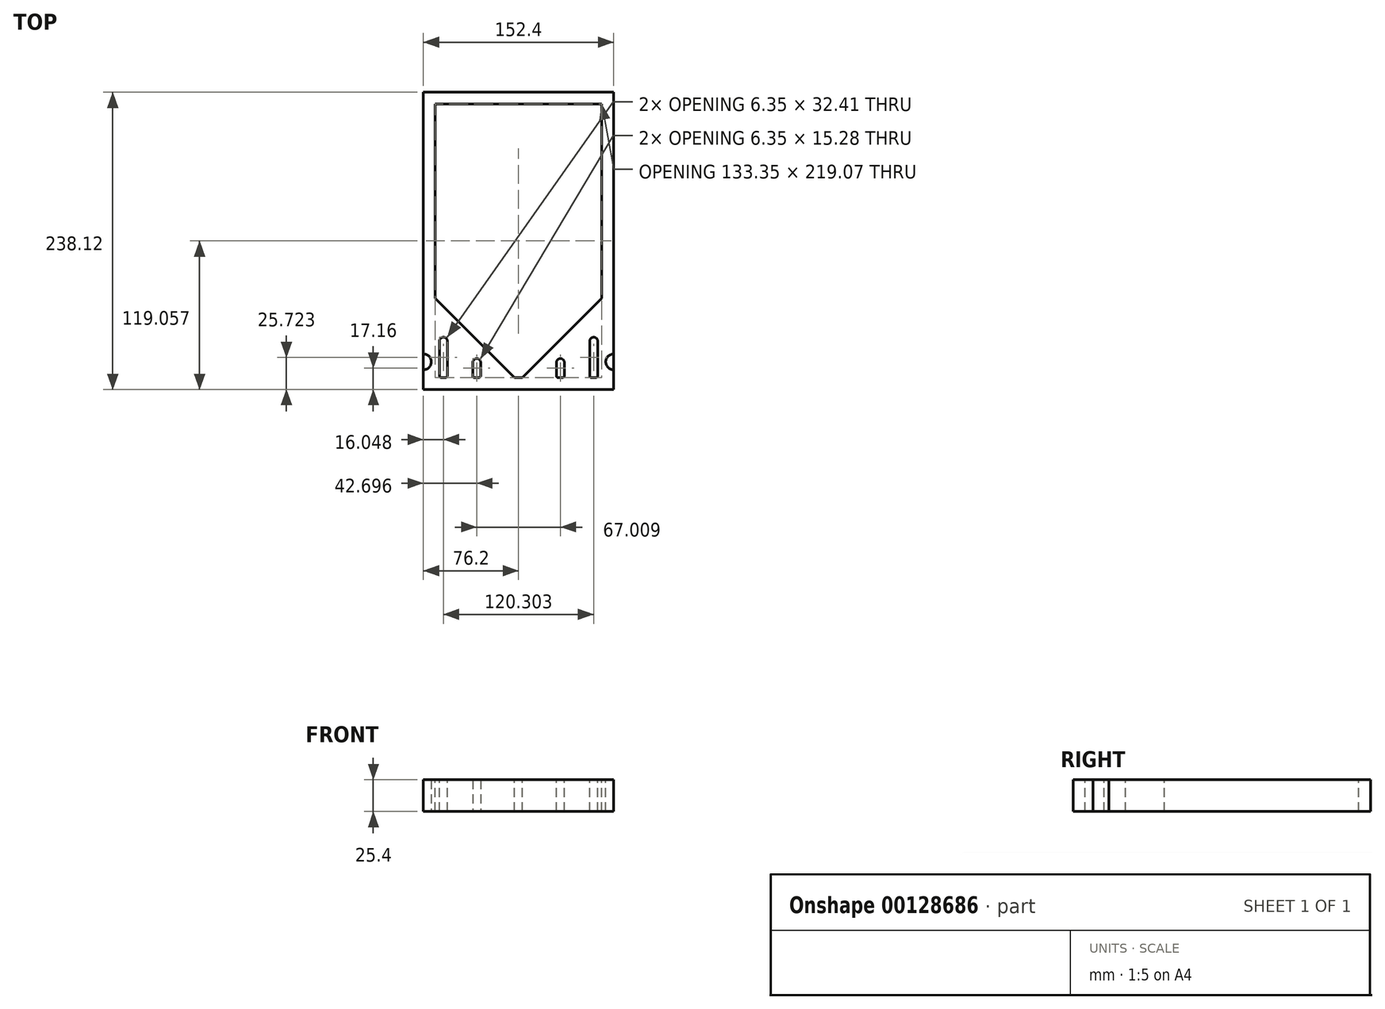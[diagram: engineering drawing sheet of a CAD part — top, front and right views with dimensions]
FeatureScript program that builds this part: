
annotation { "Feature Type Name" : "Feature", "Feature Type Description" : "" }
export const myFeature = defineFeature(function(context is Context, id is Id, definition is map)
    precondition{}
    {
        {
            var Q0;
            Q0=qCreatedBy(makeId("Top.planeOp"),FACE);
            var sketch = newSketch(context, id + "F0", { "sketchPlane" : qUnion([Q0])});
            skLineSegment(sketch, "E0", {"start": v(-76.2, 128.27) * mm, "end": v(-76.2, -109.86) * mm});
            skLineSegment(sketch, "E1", {"start": v(-76.2, -109.86) * mm, "end": v(76.2, -109.86) * mm});
            skLineSegment(sketch, "E2", {"start": v(76.2, -109.86) * mm, "end": v(76.2, 128.27) * mm});
            skLineSegment(sketch, "E3", {"start": v(76.2, 128.27) * mm, "end": v(-76.2, 128.27) * mm});
            skLineSegment(sketch, "E4.1", {"start": v(66.67, 118.75) * mm, "end": v(-66.67, 118.74) * mm});
            skLineSegment(sketch, "E5", {"start": v(-3.17, -100.33) * mm, "end": v(-66.68, -36.83) * mm});
            skLineSegment(sketch, "E6", {"start": v(-66.67, -36.83) * mm, "end": v(-66.67, 118.74) * mm});
            skLineSegment(sketch, "E7", {"start": v(66.67, 118.75) * mm, "end": v(66.67, -36.83) * mm});
            skLineSegment(sketch, "E8.MirrorCS", {"start": v(3.17, -100.33) * mm, "end": v(66.67, -36.83) * mm});
            skLineSegment(sketch, "E9", {"start": v(-3.17, -100.33) * mm, "end": v(3.17, -100.33) * mm});
            skArc(sketch, "E10", {"start": v(-76.2, -93.98) * mm, "mid": v(-69.85, -87.63) * mm, "end": v(-76.2, -81.28) * mm});
            skLineSegment(sketch, "E11", {"start": v(-56.98, -98.74) * mm, "end": v(-56.98, -71.1) * mm});
            skLineSegment(sketch, "E12.0", {"start": v(-63.33, -98.74) * mm, "end": v(-63.33, -71.1) * mm});
            skLineSegment(sketch, "E13.0", {"start": v(-30.33, -98.74) * mm, "end": v(-30.33, -88.22) * mm});
            skLineSegment(sketch, "E14.0", {"start": v(-36.68, -98.74) * mm, "end": v(-36.68, -88.22) * mm});
            skLineSegment(sketch, "E15", {"start": v(-61.74, -100.33) * mm, "end": v(-58.56, -100.33) * mm});
            skLineSegment(sketch, "E16", {"start": v(-35.1, -100.33) * mm, "end": v(-31.92, -100.33) * mm});
            skArc(sketch, "E17", {"start": v(-56.98, -71.1) * mm, "mid": v(-60.15, -67.92) * mm, "end": v(-63.33, -71.1) * mm});
            skArc(sketch, "E18", {"start": v(-30.33, -88.22) * mm, "mid": v(-33.5, -85.05) * mm, "end": v(-36.68, -88.22) * mm});
            skLineSegment(sketch, "E19.MirrorCS", {"start": v(36.68, -98.74) * mm, "end": v(36.68, -88.22) * mm});
            skLineSegment(sketch, "E20.MirrorCS", {"start": v(30.33, -98.74) * mm, "end": v(30.33, -88.22) * mm});
            skLineSegment(sketch, "E21.MirrorCS", {"start": v(35.1, -100.33) * mm, "end": v(31.92, -100.33) * mm});
            skArc(sketch, "E22.MirrorCS", {"start": v(30.33, -88.22) * mm, "mid": v(33.5, -85.05) * mm, "end": v(36.68, -88.22) * mm});
            skLineSegment(sketch, "E23.MirrorCS", {"start": v(56.98, -98.74) * mm, "end": v(56.98, -71.1) * mm});
            skLineSegment(sketch, "E24.MirrorCS", {"start": v(63.33, -98.74) * mm, "end": v(63.33, -71.1) * mm});
            skLineSegment(sketch, "E25.MirrorCS", {"start": v(61.74, -100.33) * mm, "end": v(58.56, -100.33) * mm});
            skArc(sketch, "E26.MirrorCS", {"start": v(56.98, -71.1) * mm, "mid": v(60.15, -67.92) * mm, "end": v(63.33, -71.1) * mm});
            skLineSegment(sketch, "E27", {"start": v(0, -100.33) * mm, "end": v(0, -87.84) * mm});
            skArc(sketch, "E28.MirrorCS", {"start": v(76.2, -93.98) * mm, "mid": v(69.85, -87.63) * mm, "end": v(76.2, -81.28) * mm});
            skPoint(sketch, "E29.visualSharp", {"position": v(-63.33, -100.33) * mm});
            skArc(sketch, "E29.filletArc", {"start": v(-63.33, -98.74) * mm, "mid": v(-62.86, -99.87) * mm, "end": v(-61.74, -100.33) * mm});
            skPoint(sketch, "E30.visualSharp", {"position": v(-56.98, -100.33) * mm});
            skArc(sketch, "E30.filletArc", {"start": v(-58.56, -100.33) * mm, "mid": v(-57.44, -99.87) * mm, "end": v(-56.98, -98.74) * mm});
            skPoint(sketch, "E31.visualSharp", {"position": v(-36.68, -100.33) * mm});
            skArc(sketch, "E31.filletArc", {"start": v(-36.68, -98.74) * mm, "mid": v(-36.21, -99.87) * mm, "end": v(-35.1, -100.33) * mm});
            skPoint(sketch, "E32.visualSharp", {"position": v(-30.33, -100.33) * mm});
            skArc(sketch, "E32.filletArc", {"start": v(-31.92, -100.33) * mm, "mid": v(-30.8, -99.87) * mm, "end": v(-30.33, -98.74) * mm});
            skPoint(sketch, "E33.visualSharp", {"position": v(30.33, -100.33) * mm});
            skArc(sketch, "E33.filletArc", {"start": v(30.33, -98.74) * mm, "mid": v(30.8, -99.87) * mm, "end": v(31.92, -100.33) * mm});
            skPoint(sketch, "E34.visualSharp", {"position": v(36.68, -100.33) * mm});
            skArc(sketch, "E34.filletArc", {"start": v(35.1, -100.33) * mm, "mid": v(36.21, -99.87) * mm, "end": v(36.68, -98.74) * mm});
            skPoint(sketch, "E35.visualSharp", {"position": v(56.98, -100.33) * mm});
            skArc(sketch, "E35.filletArc", {"start": v(56.98, -98.74) * mm, "mid": v(57.44, -99.87) * mm, "end": v(58.56, -100.33) * mm});
            skPoint(sketch, "E36.visualSharp", {"position": v(63.33, -100.33) * mm});
            skArc(sketch, "E36.filletArc", {"start": v(61.74, -100.33) * mm, "mid": v(62.86, -99.87) * mm, "end": v(63.33, -98.74) * mm});
            skSolve(sketch);
        }
        {
            var Q0;
            {var subQ5=sQuery(id+"F0.wireOp",EDGE,"E1");Q0=makeQuery(id+"F0.imprint","IMPRINT",FACE,{"disambiguationData":[TD([[makeQuery(id+"F0.imprint","IMPRINT",EDGE,{"derivedFrom":subQ5}),1.0]])]});}
            var Q1;
            Q1 = qConstructionFilter(qBodyType(qCreatedBy(id + "F0" ,EDGE), BodyType.WIRE), ConstructionObject.NO);
            extrude(context, id + "F1", {"entities" : qUnion([Q0]), "surfaceEntities" : qUnion([Q1]), "depth" : 25.4 * mm});
        }
        {
            var Q0;
            Q0=makeQuery(id+"F1.opExtrude","CAP_FACE",FACE,{"disambiguationData":[OSD([sQuery(id+"F0.wireOp",EDGE,"E0"),sQuery(id+"F0.wireOp",EDGE,"E1"),sQuery(id+"F0.wireOp",EDGE,"E2"),sQuery(id+"F0.wireOp",EDGE,"E3"),sQuery(id+"F0.wireOp",EDGE,"E4.1"),sQuery(id+"F0.wireOp",EDGE,"E5"),sQuery(id+"F0.wireOp",EDGE,"E6"),sQuery(id+"F0.wireOp",EDGE,"E7"),sQuery(id+"F0.wireOp",EDGE,"E8.MirrorCS"),sQuery(id+"F0.wireOp",EDGE,"E9"),sQuery(id+"F0.wireOp",EDGE,"E10"),sQuery(id+"F0.wireOp",EDGE,"E11"),sQuery(id+"F0.wireOp",EDGE,"E12.0"),sQuery(id+"F0.wireOp",EDGE,"E13.0"),sQuery(id+"F0.wireOp",EDGE,"E14.0"),sQuery(id+"F0.wireOp",EDGE,"E15"),sQuery(id+"F0.wireOp",EDGE,"E16"),sQuery(id+"F0.wireOp",EDGE,"E17"),sQuery(id+"F0.wireOp",EDGE,"E18"),sQuery(id+"F0.wireOp",EDGE,"E19.MirrorCS"),sQuery(id+"F0.wireOp",EDGE,"E20.MirrorCS"),sQuery(id+"F0.wireOp",EDGE,"E21.MirrorCS"),sQuery(id+"F0.wireOp",EDGE,"E22.MirrorCS"),sQuery(id+"F0.wireOp",EDGE,"E23.MirrorCS"),sQuery(id+"F0.wireOp",EDGE,"E24.MirrorCS"),sQuery(id+"F0.wireOp",EDGE,"E25.MirrorCS"),sQuery(id+"F0.wireOp",EDGE,"E26.MirrorCS"),sQuery(id+"F0.wireOp",EDGE,"E28.MirrorCS"),sQuery(id+"F0.wireOp",EDGE,"E29.filletArc"),sQuery(id+"F0.wireOp",EDGE,"E30.filletArc"),sQuery(id+"F0.wireOp",EDGE,"E31.filletArc"),sQuery(id+"F0.wireOp",EDGE,"E32.filletArc"),sQuery(id+"F0.wireOp",EDGE,"E33.filletArc"),sQuery(id+"F0.wireOp",EDGE,"E34.filletArc"),sQuery(id+"F0.wireOp",EDGE,"E35.filletArc"),sQuery(id+"F0.wireOp",EDGE,"E36.filletArc")])],"isStart":false});
            var sketch = newSketch(context, id + "F2", { "sketchPlane" : qUnion([Q0])});
            skLineSegment(sketch, "E37.0", {"start": v(-3.17, -100.33) * mm, "end": v(-66.67, -36.83) * mm});
            skLineSegment(sketch, "E37.1", {"start": v(-66.67, -36.83) * mm, "end": v(-66.67, 118.74) * mm});
            skLineSegment(sketch, "E37.2", {"start": v(-3.17, -100.33) * mm, "end": v(3.17, -100.33) * mm});
            skLineSegment(sketch, "E37.3", {"start": v(3.17, -100.33) * mm, "end": v(66.67, -36.83) * mm});
            skLineSegment(sketch, "E37.4", {"start": v(66.67, 118.75) * mm, "end": v(66.67, -36.83) * mm});
            skLineSegment(sketch, "E37.5", {"start": v(66.67, 118.75) * mm, "end": v(-66.67, 118.74) * mm});
            skLineSegment(sketch, "E37.6", {"start": v(-63.33, -98.74) * mm, "end": v(-63.33, -71.1) * mm});
            skLineSegment(sketch, "E37.7", {"start": v(-56.98, -98.74) * mm, "end": v(-56.98, -71.1) * mm});
            skArc(sketch, "E37.8", {"start": v(-56.98, -71.1) * mm, "mid": v(-60.15, -67.92) * mm, "end": v(-63.33, -71.1) * mm});
            skArc(sketch, "E37.9", {"start": v(-58.56, -100.33) * mm, "mid": v(-57.44, -99.87) * mm, "end": v(-56.98, -98.74) * mm});
            skLineSegment(sketch, "E37.10", {"start": v(-61.74, -100.33) * mm, "end": v(-58.56, -100.33) * mm});
            skArc(sketch, "E37.11", {"start": v(-63.33, -98.74) * mm, "mid": v(-62.86, -99.87) * mm, "end": v(-61.74, -100.33) * mm});
            skArc(sketch, "E37.12", {"start": v(-76.2, -93.98) * mm, "mid": v(-69.85, -87.63) * mm, "end": v(-76.2, -81.28) * mm});
            skLineSegment(sketch, "E37.13", {"start": v(-36.68, -98.74) * mm, "end": v(-36.68, -88.22) * mm});
            skLineSegment(sketch, "E37.14", {"start": v(-30.33, -98.74) * mm, "end": v(-30.33, -88.22) * mm});
            skArc(sketch, "E37.15", {"start": v(-30.33, -88.22) * mm, "mid": v(-33.5, -85.05) * mm, "end": v(-36.68, -88.22) * mm});
            skLineSegment(sketch, "E37.16", {"start": v(-35.1, -100.33) * mm, "end": v(-31.92, -100.33) * mm});
            skArc(sketch, "E37.17", {"start": v(-31.92, -100.33) * mm, "mid": v(-30.8, -99.87) * mm, "end": v(-30.33, -98.74) * mm});
            skArc(sketch, "E37.18", {"start": v(-36.68, -98.74) * mm, "mid": v(-36.21, -99.87) * mm, "end": v(-35.1, -100.33) * mm});
            skLineSegment(sketch, "E37.19", {"start": v(30.33, -98.74) * mm, "end": v(30.33, -88.22) * mm});
            skArc(sketch, "E37.20", {"start": v(30.33, -88.22) * mm, "mid": v(33.5, -85.05) * mm, "end": v(36.68, -88.22) * mm});
            skLineSegment(sketch, "E37.21", {"start": v(36.68, -98.74) * mm, "end": v(36.68, -88.22) * mm});
            skLineSegment(sketch, "E37.22", {"start": v(35.1, -100.33) * mm, "end": v(31.92, -100.33) * mm});
            skArc(sketch, "E37.23", {"start": v(35.1, -100.33) * mm, "mid": v(36.21, -99.87) * mm, "end": v(36.68, -98.74) * mm});
            skArc(sketch, "E37.24", {"start": v(30.33, -98.74) * mm, "mid": v(30.8, -99.87) * mm, "end": v(31.92, -100.33) * mm});
            skLineSegment(sketch, "E37.25", {"start": v(63.33, -98.74) * mm, "end": v(63.33, -71.1) * mm});
            skLineSegment(sketch, "E37.26", {"start": v(56.98, -98.74) * mm, "end": v(56.98, -71.1) * mm});
            skArc(sketch, "E37.27", {"start": v(56.98, -71.1) * mm, "mid": v(60.15, -67.92) * mm, "end": v(63.33, -71.1) * mm});
            skLineSegment(sketch, "E37.28", {"start": v(61.74, -100.33) * mm, "end": v(58.56, -100.33) * mm});
            skArc(sketch, "E37.29", {"start": v(61.74, -100.33) * mm, "mid": v(62.86, -99.87) * mm, "end": v(63.33, -98.74) * mm});
            skArc(sketch, "E37.30", {"start": v(56.98, -98.74) * mm, "mid": v(57.44, -99.87) * mm, "end": v(58.56, -100.33) * mm});
            skArc(sketch, "E37.31", {"start": v(76.2, -93.98) * mm, "mid": v(69.85, -87.63) * mm, "end": v(76.2, -81.28) * mm});
            skLineSegment(sketch, "E38", {"start": v(-76.2, -93.98) * mm, "end": v(-76.2, -81.28) * mm});
            skLineSegment(sketch, "E39", {"start": v(76.2, -93.98) * mm, "end": v(76.2, -81.28) * mm});
            skSolve(sketch);
        }
        {
            var Q0;
            Q0 = qSketchRegion(id + "F2", true);
            extrude(context, id + "F3", {"entities" : qUnion([Q0]), "oppositeDirection" : true, "depth" : 25.4 * mm});
        }
    });
